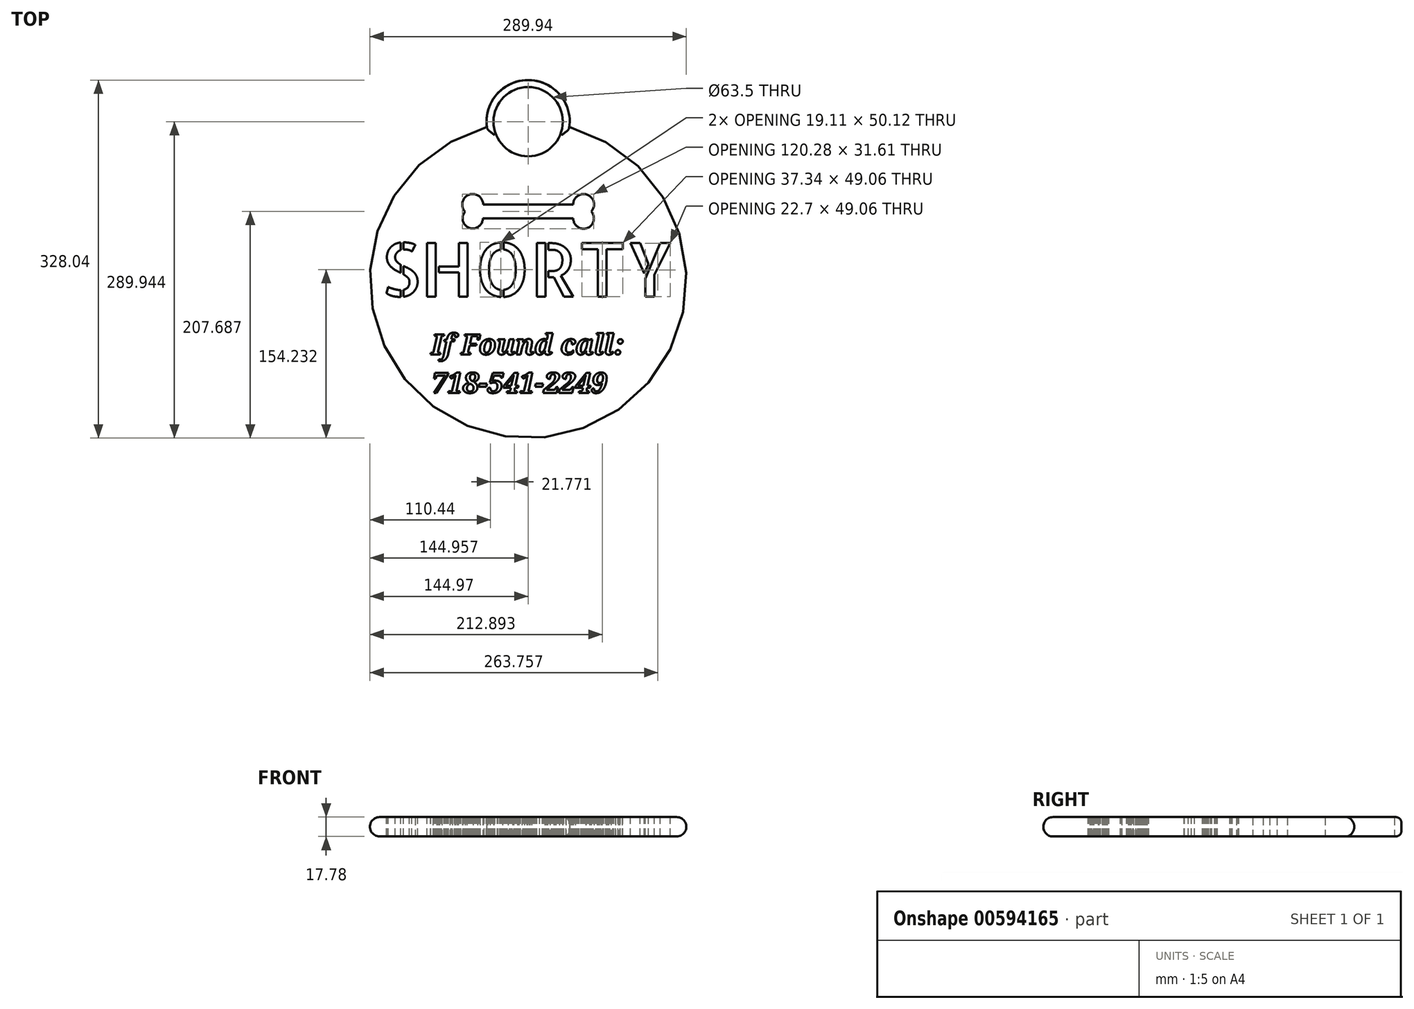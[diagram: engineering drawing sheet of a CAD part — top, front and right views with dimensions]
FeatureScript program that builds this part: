
annotation { "Feature Type Name" : "Feature", "Feature Type Description" : "" }
export const myFeature = defineFeature(function(context is Context, id is Id, definition is map)
    precondition{}
    {
        {
            var Q0;
            Q0=qCreatedBy(makeId("Top.planeOp"),FACE);
            var sketch = newSketch(context, id + "F0", { "sketchPlane" : qUnion([Q0])});
            skArc(sketch, "E0", {"start": v(-37.77, 139.97) * mm, "mid": v(0, -144.97) * mm, "end": v(37.77, 139.97) * mm});
            skCircle(sketch, "E1", {"center": v(0, 144.97) * mm, "radius": 31.75 * mm});
            skArc(sketch, "E2", {"start": v(37.77, 139.97) * mm, "mid": v(0, 183.07) * mm, "end": v(-37.77, 139.97) * mm});
            skLineSegment(sketch, "E3", {"start": v(43.62, 62.65) * mm, "end": v(43.79, 62.65) * mm});
            skLineSegment(sketch, "E4", {"start": v(-43.63, 62.65) * mm, "end": v(-44.05, 62.65) * mm});
            skLineSegment(sketch, "E5.0", {"start": v(0, 56.3) * mm, "end": v(41.34, 56.3) * mm});
            skLineSegment(sketch, "E6.0", {"start": v(0, 69) * mm, "end": v(-41.22, 69) * mm});
            skLineSegment(sketch, "E7.0", {"start": v(0, 69) * mm, "end": v(41.22, 69) * mm});
            skLineSegment(sketch, "E8.0", {"start": v(0, 56.3) * mm, "end": v(-41.53, 56.3) * mm});
            skArc(sketch, "E9", {"start": v(-43.84, 62.42) * mm, "mid": v(-43.73, 62.54) * mm, "end": v(-43.63, 62.65) * mm});
            skArc(sketch, "E10", {"start": v(-57.76, 62.42) * mm, "mid": v(-54.07, 47.63) * mm, "end": v(-41.53, 56.3) * mm});
            skArc(sketch, "E11", {"start": v(43.62, 62.65) * mm, "mid": v(43.66, 62.6) * mm, "end": v(43.7, 62.56) * mm});
            skArc(sketch, "E12", {"start": v(43.79, 62.65) * mm, "mid": v(43.74, 62.6) * mm, "end": v(43.7, 62.56) * mm});
            skArc(sketch, "E13.trimOffspring", {"start": v(-41.22, 69) * mm, "mid": v(-54.34, 77.9) * mm, "end": v(-57.76, 62.42) * mm});
            skArc(sketch, "E14.trimOffspring", {"start": v(-43.84, 62.42) * mm, "mid": v(-43.95, 62.54) * mm, "end": v(-44.05, 62.65) * mm});
            skArc(sketch, "E15.trimOffspring", {"start": v(57.9, 62.56) * mm, "mid": v(54.25, 77.94) * mm, "end": v(41.22, 69) * mm});
            skArc(sketch, "E16.trimOffspring", {"start": v(41.34, 56.3) * mm, "mid": v(54.15, 47.45) * mm, "end": v(57.9, 62.56) * mm});
            skPoint(sketch, "E17.orphan", {"position": v(0, 113.22) * mm});
            skSolve(sketch);
        }
        {
            var Q0;
            Q0=makeQuery(id+"F0.imprint","IMPRINT",FACE,{"disambiguationData":[TD([[makeQuery(id+"F0.imprint","IMPRINT",EDGE,{"derivedFrom":sQuery(id+"F0.wireOp",EDGE,"E0")}),1.0]])]});
            extrude(context, id + "F1", {"entities" : qUnion([Q0]), "depth" : 17.78 * mm, "offsetDistance" : 25.4 * mm});
        }
        {
            var Q0;
            Q0=makeQuery(id+"F1.opExtrude","CAP_FACE",FACE,{"disambiguationData":[OSD([sQuery(id+"F0.wireOp",EDGE,"E0")])],"isStart":false});
            var sketch = newSketch(context, id + "F2", { "sketchPlane" : qUnion([Q0])});
            skText(sketch, "E18", { "text": "SHORTY", "fontName": "AllertaStencil-Regular.ttf"});
            const initialGuessF2  = {"E18": [-0.13515, -0.01547, 1, 0, 0.04908]};
            skSetInitialGuess(sketch, initialGuessF2);
            skSolve(sketch);
        }
        {
            var Q0;
            Q0 = qSketchRegion(id + "F2", true);
            extrude(context, id + "F3", {"entities" : qUnion([Q0]), "operationType" : NewBodyOperationType.REMOVE, "oppositeDirection" : true, "depth" : 25.4 * mm, "offsetDistance" : 25.4 * mm});
        }
        {
            var Q0;
            Q0=makeQuery(id+"F1.opExtrude","CAP_FACE",FACE,{"disambiguationData":[OSD([sQuery(id+"F0.wireOp",EDGE,"E0")])],"isStart":false});
            var sketch = newSketch(context, id + "F4", { "sketchPlane" : qUnion([Q0])});
            skText(sketch, "E19", { "text": "If Found call:\n718-541-2249", "fontName": "NotoSerif-BoldItalic.ttf"});
            const initialGuessF4  = {"E19": [-0.0889, -0.06843, 1, 0, 0.01866]};
            skSetInitialGuess(sketch, initialGuessF4);
            skSolve(sketch);
        }
        {
            var Q0;
            Q0 = qSketchRegion(id + "F4", true);
            extrude(context, id + "F5", {"entities" : qUnion([Q0]), "operationType" : NewBodyOperationType.REMOVE, "oppositeDirection" : true, "depth" : 25.4 * mm, "offsetDistance" : 25.4 * mm});
        }
        {
            var Q0;
            Q0=makeQuery(id+"F1.opExtrude","CAP_EDGE",EDGE,{"disambiguationData":[OSD([sQuery(id+"F0.wireOp",EDGE,"E0")])],"isStart":false});
            var Q1;
            Q1=makeQuery(id+"F1.opExtrude","CAP_EDGE",EDGE,{"disambiguationData":[OSD([sQuery(id+"F0.wireOp",EDGE,"E0")])],"isStart":true});
            fillet(context, id + "F6", {"entities" : qUnion([Q0, Q1]), "radius" : 8.9 * mm, "tangentPropagation" : true, "allowEdgeOverflow" : false});
        }
        {
            var Q0;
            Q0=makeQuery(id+"F1.opExtrude","CAP_EDGE",EDGE,{"disambiguationData":[OSD([sQuery(id+"F0.wireOp",EDGE,"E2")])],"isStart":false});
            var Q1;
            Q1=makeQuery(id+"F1.opExtrude","CAP_EDGE",EDGE,{"disambiguationData":[OSD([sQuery(id+"F0.wireOp",EDGE,"E2")])],"isStart":true});
            fillet(context, id + "F7", {"entities" : qUnion([Q0, Q1]), "radius" : 5.08 * mm, "tangentPropagation" : true, "allowEdgeOverflow" : false});
        }
    });
